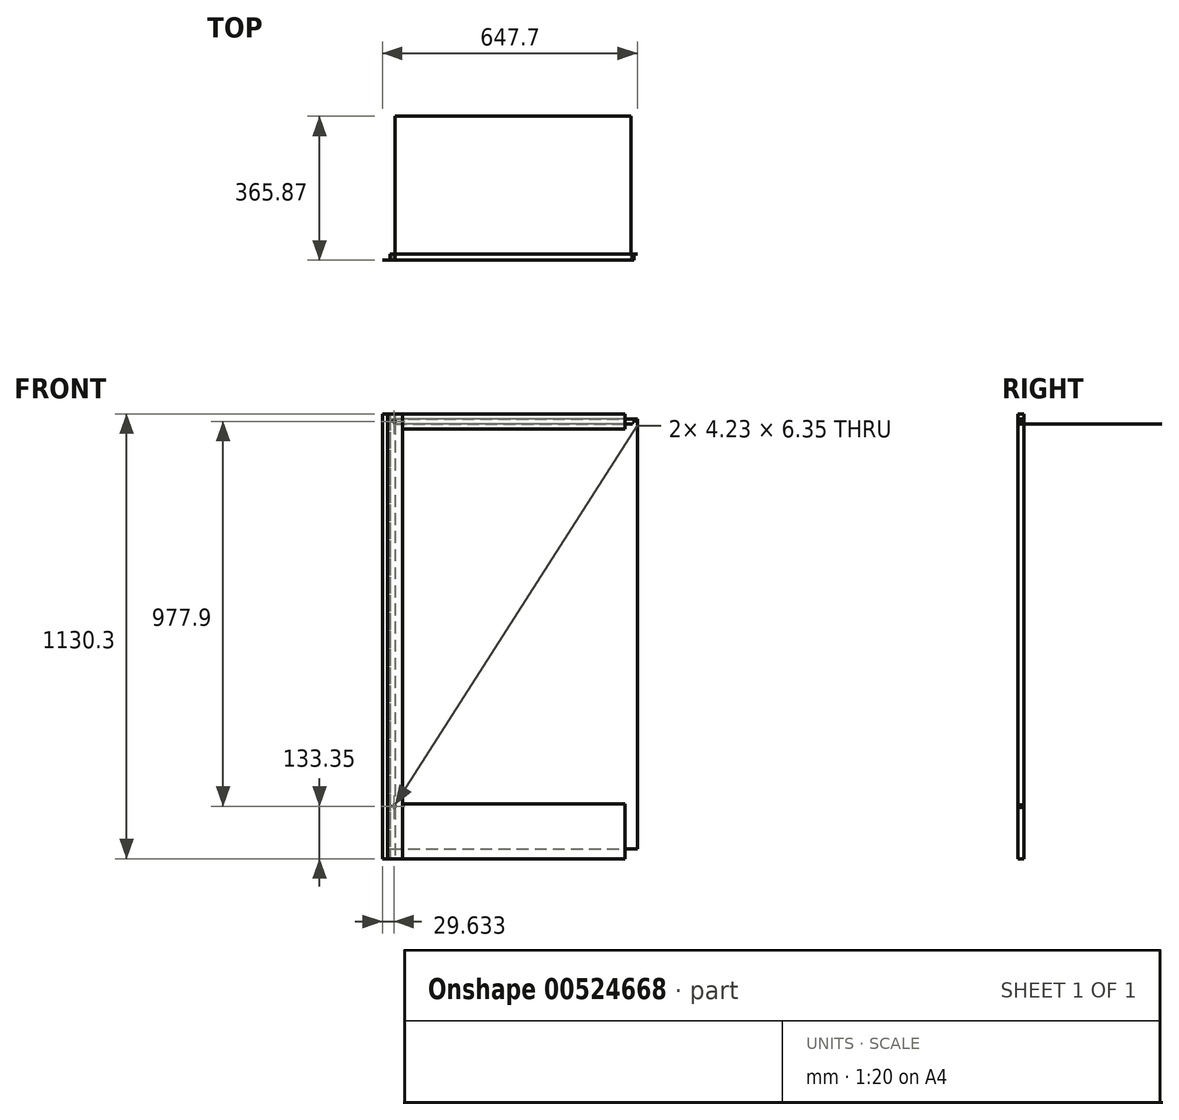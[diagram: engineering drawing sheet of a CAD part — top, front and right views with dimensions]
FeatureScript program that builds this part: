
annotation { "Feature Type Name" : "Feature", "Feature Type Description" : "" }
export const myFeature = defineFeature(function(context is Context, id is Id, definition is map)
    precondition{}
    {
        {
            assignVariable(context, id + "F0", {"name" : "Debth", "anyValue" : 15.5});
        }
        {
            assignVariable(context, id + "F1", {"name" : "StileRailThickness", "anyValue" : .75});
        }
        {
            var Q0;
            Q0=qCreatedBy(makeId("Front.planeOp"),FACE);
            var sketch = newSketch(context, id + "F2", { "sketchPlane" : qUnion([Q0])});
            skLineSegment(sketch, "E0.bottom", {"start": v(0, 0) * mm, "end": v(38.1, 0) * mm});
            skLineSegment(sketch, "E0.top", {"start": v(0, 1130.3) * mm, "end": v(38.1, 1130.3) * mm});
            skLineSegment(sketch, "E0.left", {"start": v(0, 0) * mm, "end": v(0, 1130.3) * mm});
            skLineSegment(sketch, "E0.right", {"start": v(38.1, 0) * mm, "end": v(38.1, 1130.3) * mm});
            skSolve(sketch);
        }
        {
            var Q0;
            Q0 = qSketchRegion(id + "F2", true);
            extrude(context, id + "F3", {"entities" : qUnion([Q0]), "depth" : (getVariable(context, 'StileRailThickness')) * mm, "offsetDistance" : 25.4 * mm});
        }
        {
            var Q0;
            Q0=qCreatedBy(makeId("Front.planeOp"),FACE);
            var sketch = newSketch(context, id + "F4", { "sketchPlane" : qUnion([Q0])});
            skLineSegment(sketch, "E1.bottom", {"start": v(38.1, 1130.3) * mm, "end": v(603.25, 1130.3) * mm});
            skLineSegment(sketch, "E1.top", {"start": v(38.1, 1092.2) * mm, "end": v(603.25, 1092.2) * mm});
            skLineSegment(sketch, "E1.left", {"start": v(38.1, 1130.3) * mm, "end": v(38.1, 1092.2) * mm});
            skLineSegment(sketch, "E1.right", {"start": v(603.25, 1130.3) * mm, "end": v(603.25, 1092.2) * mm});
            skSolve(sketch);
        }
        {
            var Q0;
            Q0 = qSketchRegion(id + "F4", true);
            extrude(context, id + "F5", {"entities" : qUnion([Q0]), "depth" : (getVariable(context, 'StileRailThickness')) * mm, "offsetDistance" : 25.4 * mm});
        }
        {
            assignVariable(context, id + "F6", {"name" : "SideThickness", "anyValue" : .5});
        }
        {
            assignVariable(context, id + "F7", {"name" : "BackThickness", "anyValue" : .25});
        }
        {
            var Q0;
            Q0=makeQuery(id+"F3.opExtrude","CAP_FACE",FACE,{"disambiguationData":[OSD([sQuery(id+"F2.wireOp",EDGE,"E0.bottom"),sQuery(id+"F2.wireOp",EDGE,"E0.top"),sQuery(id+"F2.wireOp",EDGE,"E0.left"),sQuery(id+"F2.wireOp",EDGE,"E0.right")])],"isStart":true});
            var sketch = newSketch(context, id + "F8", { "sketchPlane" : qUnion([Q0])});
            skLineSegment(sketch, "E2", {"start": v(-12.7, 1130.3) * mm, "end": v(-12.7, 622.83) * mm, "construction": true});
            skLineSegment(sketch, "E3.bottom", {"start": v(-19.05, 1130.3) * mm, "end": v(-6.35, 1130.3) * mm});
            skLineSegment(sketch, "E3.top", {"start": v(-19.05, 0) * mm, "end": v(-6.35, 0) * mm});
            skLineSegment(sketch, "E3.left", {"start": v(-19.05, 1130.3) * mm, "end": v(-19.05, 0) * mm});
            skLineSegment(sketch, "E3.right", {"start": v(-6.35, 1130.3) * mm, "end": v(-6.35, 0) * mm});
            skSolve(sketch);
        }
        {
            var Q0;
            Q0 = qSketchRegion(id + "F8", true);
            extrude(context, id + "F9", {"entities" : qUnion([Q0]), "depth" : (getVariable(context, 'Debth') - getVariable(context, 'StileRailThickness') - getVariable(context, 'BackThickness')) * mm, "offsetDistance" : 25.4 * mm});
        }
        {
            var Q0;
            Q0=makeQuery(id+"F5.opExtrude","CAP_FACE",FACE,{"disambiguationData":[OSD([sQuery(id+"F4.wireOp",EDGE,"E1.bottom"),sQuery(id+"F4.wireOp",EDGE,"E1.top"),sQuery(id+"F4.wireOp",EDGE,"E1.left"),sQuery(id+"F4.wireOp",EDGE,"E1.right")])],"isStart":true});
            var sketch = newSketch(context, id + "F10", { "sketchPlane" : qUnion([Q0])});
            skLineSegment(sketch, "E4.bottom", {"start": v(-622.3, 1117.6) * mm, "end": v(-19.05, 1117.6) * mm});
            skLineSegment(sketch, "E4.top", {"start": v(-622.3, 1104.9) * mm, "end": v(-19.05, 1104.9) * mm});
            skLineSegment(sketch, "E4.left", {"start": v(-622.3, 1117.6) * mm, "end": v(-622.3, 1104.9) * mm});
            skLineSegment(sketch, "E4.right", {"start": v(-19.05, 1117.6) * mm, "end": v(-19.05, 1104.9) * mm});
            skLineSegment(sketch, "E5", {"start": v(-320.67, 1130.3) * mm, "end": v(-320.67, 1092.2) * mm, "construction": true});
            skLineSegment(sketch, "E6", {"start": v(-19.05, 1114.43) * mm, "end": v(-14.82, 1114.43) * mm});
            skLineSegment(sketch, "E7", {"start": v(-14.82, 1114.43) * mm, "end": v(-14.82, 1108.07) * mm});
            skLineSegment(sketch, "E8", {"start": v(-14.82, 1108.07) * mm, "end": v(-19.05, 1108.07) * mm});
            skLineSegment(sketch, "E9", {"start": v(-19.05, 1111.25) * mm, "end": v(-622.3, 1111.25) * mm, "construction": true});
            skLineSegment(sketch, "E10", {"start": v(-622.3, 1114.42) * mm, "end": v(-626.53, 1114.42) * mm});
            skLineSegment(sketch, "E11", {"start": v(-626.53, 1114.43) * mm, "end": v(-626.53, 1108.07) * mm});
            skLineSegment(sketch, "E12", {"start": v(-626.53, 1108.07) * mm, "end": v(-622.3, 1108.07) * mm});
            skSolve(sketch);
        }
        {
            var Q0;
            Q0 = qSketchRegion(id + "F10", true);
            var Q1;
            Q1=makeQuery(id+"F9.opExtrude","CAP_FACE",FACE,{"disambiguationData":[OSD([sQuery(id+"F8.wireOp",EDGE,"E3.bottom"),sQuery(id+"F8.wireOp",EDGE,"E3.top"),sQuery(id+"F8.wireOp",EDGE,"E3.left"),sQuery(id+"F8.wireOp",EDGE,"E3.right")])],"isStart":false});
            extrude(context, id + "F11", {"entities" : qUnion([Q0]), "endBound" : BoundingType.UP_TO_SURFACE, "depth" : 25.4 * mm, "endBoundEntityFace" : qUnion([Q1]), "offsetDistance" : 25.4 * mm});
        }
        {
            var Q0;
            Q0=makeQuery(id+"F11.opExtrude","SWEPT_FACE",FACE,{"disambiguationData":[OSD([sQuery(id+"F10.wireOp",EDGE,"E4.top")])]});
            var sketch = newSketch(context, id + "F12", { "sketchPlane" : qUnion([Q0])});
            skLineSegment(sketch, "E13.bottom", {"start": v(19.05, 0) * mm, "end": v(619.12, 0) * mm});
            skLineSegment(sketch, "E13.top", {"start": v(19.05, -365.12) * mm, "end": v(619.12, -365.12) * mm});
            skLineSegment(sketch, "E13.left", {"start": v(19.05, 0) * mm, "end": v(19.05, -365.12) * mm});
            skLineSegment(sketch, "E13.right", {"start": v(619.12, 0) * mm, "end": v(619.12, -365.12) * mm});
            skSolve(sketch);
        }
        {
            var Q0;
            Q0 = qSketchRegion(id + "F12", true);
            extrude(context, id + "F13", {"entities" : qUnion([Q0]), "depth" : (getVariable(context, 'SideThickness')) * mm, "offsetDistance" : 25.4 * mm});
        }
        {
            var Q0;
            Q0=makeQuery(id+"F9.opExtrude","CAP_FACE",FACE,{"disambiguationData":[OSD([sQuery(id+"F8.wireOp",EDGE,"E3.bottom"),sQuery(id+"F8.wireOp",EDGE,"E3.top"),sQuery(id+"F8.wireOp",EDGE,"E3.left"),sQuery(id+"F8.wireOp",EDGE,"E3.right")])],"isStart":false});
            var sketch = newSketch(context, id + "F14", { "sketchPlane" : qUnion([Q0])});
            skLineSegment(sketch, "E14", {"start": v(-320.67, 1130.3) * mm, "end": v(-320.67, 763.53) * mm, "construction": true});
            skLineSegment(sketch, "E15.bottom", {"start": v(-6.35, 1117.6) * mm, "end": v(-635, 1117.6) * mm});
            skLineSegment(sketch, "E15.top", {"start": v(-6.35, 25.4) * mm, "end": v(-635, 25.4) * mm});
            skLineSegment(sketch, "E15.left", {"start": v(-6.35, 1117.6) * mm, "end": v(-6.35, 25.4) * mm});
            skLineSegment(sketch, "E15.right", {"start": v(-635, 1117.6) * mm, "end": v(-635, 25.4) * mm});
            skSolve(sketch);
        }
        {
            var Q0;
            Q0 = qSketchRegion(id + "F14", true);
            extrude(context, id + "F15", {"entities" : qUnion([Q0]), "depth" : (getVariable(context, 'BackThickness')) * mm, "offsetDistance" : 25.4 * mm});
        }
        {
            var Q0;
            Q0=makeQuery(id+"F3.opExtrude","CAP_FACE",FACE,{"disambiguationData":[OSD([sQuery(id+"F2.wireOp",EDGE,"E0.bottom"),sQuery(id+"F2.wireOp",EDGE,"E0.top"),sQuery(id+"F2.wireOp",EDGE,"E0.left"),sQuery(id+"F2.wireOp",EDGE,"E0.right")])],"isStart":false});
            var sketch = newSketch(context, id + "F16", { "sketchPlane" : qUnion([Q0])});
            skLineSegment(sketch, "E16.bottom", {"start": v(38.1, 139.7) * mm, "end": v(603.25, 139.7) * mm});
            skLineSegment(sketch, "E16.top", {"start": v(38.1, 0) * mm, "end": v(603.25, 0) * mm});
            skLineSegment(sketch, "E16.left", {"start": v(38.1, 139.7) * mm, "end": v(38.1, 0) * mm});
            skLineSegment(sketch, "E16.right", {"start": v(603.25, 139.7) * mm, "end": v(603.25, 0) * mm});
            skSolve(sketch);
        }
        {
            var Q0;
            Q0 = qSketchRegion(id + "F16", true);
            var Q1;
            Q1=makeQuery(id+"F3.opExtrude","CAP_FACE",FACE,{"disambiguationData":[OSD([sQuery(id+"F2.wireOp",EDGE,"E0.bottom"),sQuery(id+"F2.wireOp",EDGE,"E0.top"),sQuery(id+"F2.wireOp",EDGE,"E0.left"),sQuery(id+"F2.wireOp",EDGE,"E0.right")])],"isStart":true});
            extrude(context, id + "F17", {"entities" : qUnion([Q0]), "endBound" : BoundingType.UP_TO_SURFACE, "oppositeDirection" : true, "depth" : 25.4 * mm, "endBoundEntityFace" : qUnion([Q1]), "offsetDistance" : 25.4 * mm});
        }
        {
            var Q0;
            Q0=makeQuery(id+"F9.opExtrude","CAP_FACE",FACE,{"disambiguationData":[OSD([sQuery(id+"F8.wireOp",EDGE,"E3.bottom"),sQuery(id+"F8.wireOp",EDGE,"E3.top"),sQuery(id+"F8.wireOp",EDGE,"E3.left"),sQuery(id+"F8.wireOp",EDGE,"E3.right")])],"isStart":false});
            var sketch = newSketch(context, id + "F18", { "sketchPlane" : qUnion([Q0])});
            skLineSegment(sketch, "E17.bottom", {"start": v(-19.05, 1114.43) * mm, "end": v(-14.82, 1114.43) * mm});
            skLineSegment(sketch, "E17.top", {"start": v(-19.05, 1108.07) * mm, "end": v(-14.82, 1108.07) * mm});
            skLineSegment(sketch, "E17.left", {"start": v(-19.05, 1114.43) * mm, "end": v(-19.05, 1108.07) * mm});
            skLineSegment(sketch, "E17.right", {"start": v(-14.82, 1114.43) * mm, "end": v(-14.82, 1108.07) * mm});
            skLineSegment(sketch, "E18", {"start": v(-14.82, 1108.07) * mm, "end": v(-14.82, 0) * mm, "construction": true});
            skLineSegment(sketch, "E19.bottom", {"start": v(-19.05, 136.52) * mm, "end": v(-14.82, 136.52) * mm});
            skLineSegment(sketch, "E19.top", {"start": v(-19.05, 130.17) * mm, "end": v(-14.82, 130.17) * mm});
            skLineSegment(sketch, "E19.left", {"start": v(-19.05, 136.52) * mm, "end": v(-19.05, 130.17) * mm});
            skLineSegment(sketch, "E19.right", {"start": v(-14.82, 136.52) * mm, "end": v(-14.82, 130.17) * mm});
            skSolve(sketch);
        }
        {
            var Q0;
            Q0 = qSketchRegion(id + "F18", true);
            extrude(context, id + "F19", {"entities" : qUnion([Q0]), "operationType" : NewBodyOperationType.REMOVE, "endBound" : BoundingType.THROUGH_ALL, "oppositeDirection" : true, "depth" : 25.4 * mm, "offsetDistance" : 25.4 * mm});
        }
        {
            var Q0;
            Q0=makeQuery(id+"F3.opExtrude","CAP_FACE",FACE,{"disambiguationData":[OSD([sQuery(id+"F2.wireOp",EDGE,"E0.bottom"),sQuery(id+"F2.wireOp",EDGE,"E0.top"),sQuery(id+"F2.wireOp",EDGE,"E0.left"),sQuery(id+"F2.wireOp",EDGE,"E0.right")])],"isStart":false});
            var sketch = newSketch(context, id + "F20", { "sketchPlane" : qUnion([Q0])});
            skLineSegment(sketch, "E20.bottom", {"start": v(0, 1130.3) * mm, "end": v(-12.7, 1130.3) * mm});
            skLineSegment(sketch, "E20.top", {"start": v(0, 0) * mm, "end": v(-12.7, 0) * mm});
            skLineSegment(sketch, "E20.left", {"start": v(0, 1130.3) * mm, "end": v(0, 0) * mm});
            skLineSegment(sketch, "E20.right", {"start": v(-12.7, 1130.3) * mm, "end": v(-12.7, 0) * mm});
            skSolve(sketch);
        }
        {
            var Q0;
            Q0 = qSketchRegion(id + "F20", true);
            var Q1;
            Q1=makeQuery(id+"F5.opExtrude","CAP_FACE",FACE,{"disambiguationData":[OSD([sQuery(id+"F4.wireOp",EDGE,"E1.bottom"),sQuery(id+"F4.wireOp",EDGE,"E1.top"),sQuery(id+"F4.wireOp",EDGE,"E1.left"),sQuery(id+"F4.wireOp",EDGE,"E1.right")])],"isStart":true});
            extrude(context, id + "F21", {"entities" : qUnion([Q0]), "endBound" : BoundingType.UP_TO_SURFACE, "oppositeDirection" : true, "depth" : 25.4 * mm, "endBoundEntityFace" : qUnion([Q1]), "offsetDistance" : 25.4 * mm});
        }
    });
